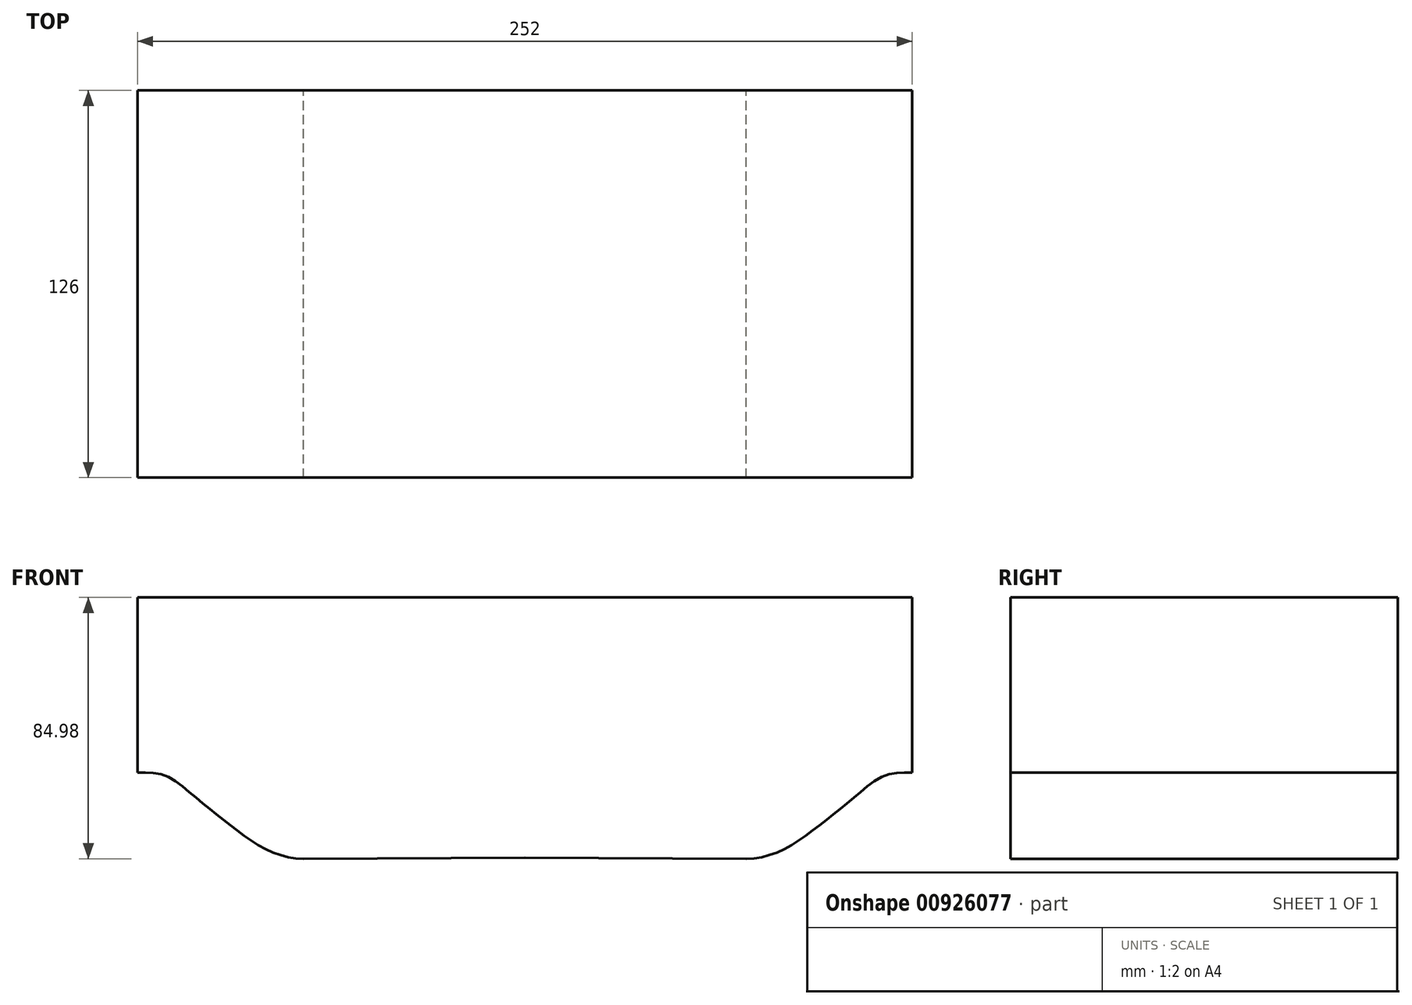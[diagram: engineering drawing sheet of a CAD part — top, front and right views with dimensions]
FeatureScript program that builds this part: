
annotation { "Feature Type Name" : "Feature", "Feature Type Description" : "" }
export const myFeature = defineFeature(function(context is Context, id is Id, definition is map)
    precondition{}
    {
        {
            var Q0;
            Q0=qCreatedBy(makeId("Front.planeOp"),FACE);
            var sketch = newSketch(context, id + "F0", { "sketchPlane" : qUnion([Q0])});
            skPoint(sketch, "E0", {"position": v(0, 28) * mm});
            skPoint(sketch, "E1", {"position": v(2, 28) * mm});
            skPoint(sketch, "E2", {"position": v(4, 27.97) * mm});
            skPoint(sketch, "E3", {"position": v(6, 27.79) * mm});
            skPoint(sketch, "E4", {"position": v(8, 27.35) * mm});
            skPoint(sketch, "E5", {"position": v(10, 26.56) * mm});
            skPoint(sketch, "E6", {"position": v(12, 25.41) * mm});
            skPoint(sketch, "E7", {"position": v(14, 24) * mm});
            skPoint(sketch, "E8", {"position": v(16, 22.41) * mm});
            skPoint(sketch, "E9", {"position": v(18, 20.71) * mm});
            skPoint(sketch, "E10", {"position": v(20, 19) * mm});
            skPoint(sketch, "E11", {"position": v(22, 17.33) * mm});
            skPoint(sketch, "E12", {"position": v(24, 15.7) * mm});
            skPoint(sketch, "E13", {"position": v(26, 14.11) * mm});
            skPoint(sketch, "E14", {"position": v(28, 12.55) * mm});
            skPoint(sketch, "E15", {"position": v(30, 11) * mm});
            skPoint(sketch, "E16", {"position": v(32, 9.47) * mm});
            skPoint(sketch, "E17", {"position": v(34, 7.97) * mm});
            skPoint(sketch, "E18", {"position": v(36, 6.54) * mm});
            skPoint(sketch, "E19", {"position": v(38, 5.21) * mm});
            skPoint(sketch, "E20", {"position": v(40, 4) * mm});
            skPoint(sketch, "E21", {"position": v(42, 2.95) * mm});
            skPoint(sketch, "E22", {"position": v(44, 2.05) * mm});
            skPoint(sketch, "E23", {"position": v(46, 1.32) * mm});
            skPoint(sketch, "E24", {"position": v(48, 0.74) * mm});
            skPoint(sketch, "E25", {"position": v(50, 0.33) * mm});
            skPoint(sketch, "E26", {"position": v(52, 0.08) * mm});
            skPoint(sketch, "E27", {"position": v(54, 0) * mm});
            skLineSegment(sketch, "E28", {"start": v(0, 28) * mm, "end": v(0, 84.98) * mm});
            skLineSegment(sketch, "E29", {"start": v(0, 84.98) * mm, "end": v(126, 84.98) * mm});
            skLineSegment(sketch, "E30", {"start": v(54, 0) * mm, "end": v(126, 0.29) * mm});
            skLineSegment(sketch, "E31", {"start": v(126, 84.98) * mm, "end": v(126, 0.29) * mm});
            skFitSpline(sketch, "E32", {"points": [v(0, 28) * mm, v(2, 28) * mm, v(4, 27.97) * mm, v(6, 27.79) * mm, v(8, 27.35) * mm, v(10, 26.56) * mm, v(12, 25.41) * mm, v(14, 24) * mm, v(16, 22.41) * mm, v(18, 20.71) * mm, v(20, 19) * mm, v(22, 17.33) * mm, v(24, 15.7) * mm, v(26, 14.11) * mm, v(28, 12.55) * mm, v(30, 11) * mm, v(32, 9.47) * mm, v(34, 7.97) * mm, v(36, 6.54) * mm, v(38, 5.21) * mm, v(40, 4) * mm, v(42, 2.95) * mm, v(44, 2.05) * mm, v(46, 1.32) * mm, v(48, 0.74) * mm, v(50, 0.33) * mm, v(52, 0.08) * mm, v(54, 0) * mm], "startDerivative": vector(58.03, 0.03) * mm, "endDerivative": vector(58.04, -1.26) * mm});
            skSolve(sketch);
        }
        {
            var Q0;
            Q0=qSketchRegion(id+"F0",true);
            extrude(context, id + "F1", {"entities" : qUnion([Q0]), "depth" : 126 * mm, "offsetDistance" : 25 * mm});
        }
        {
            var Q0;
            Q0=makeQuery(id+"F1.opExtrude","SWEPT_BODY",BODY,{"disambiguationData":[OSD([sQuery(id+"F0.wireOp",EDGE,"E28"),sQuery(id+"F0.wireOp",EDGE,"E29"),sQuery(id+"F0.wireOp",EDGE,"E30"),sQuery(id+"F0.wireOp",EDGE,"E31"),sQuery(id+"F0.wireOp",EDGE,"E32")])]});
            var Q1;
            Q1=makeQuery(id+"F1.opExtrude","SWEPT_FACE",FACE,{"disambiguationData":[OSD([sQuery(id+"F0.wireOp",EDGE,"E31")])]});
            mirror(context, id + "F2", {"operationType" : NewBodyOperationType.ADD, "entities" : qUnion([Q0]), "mirrorPlane" : qUnion([Q1])});
        }
    });
